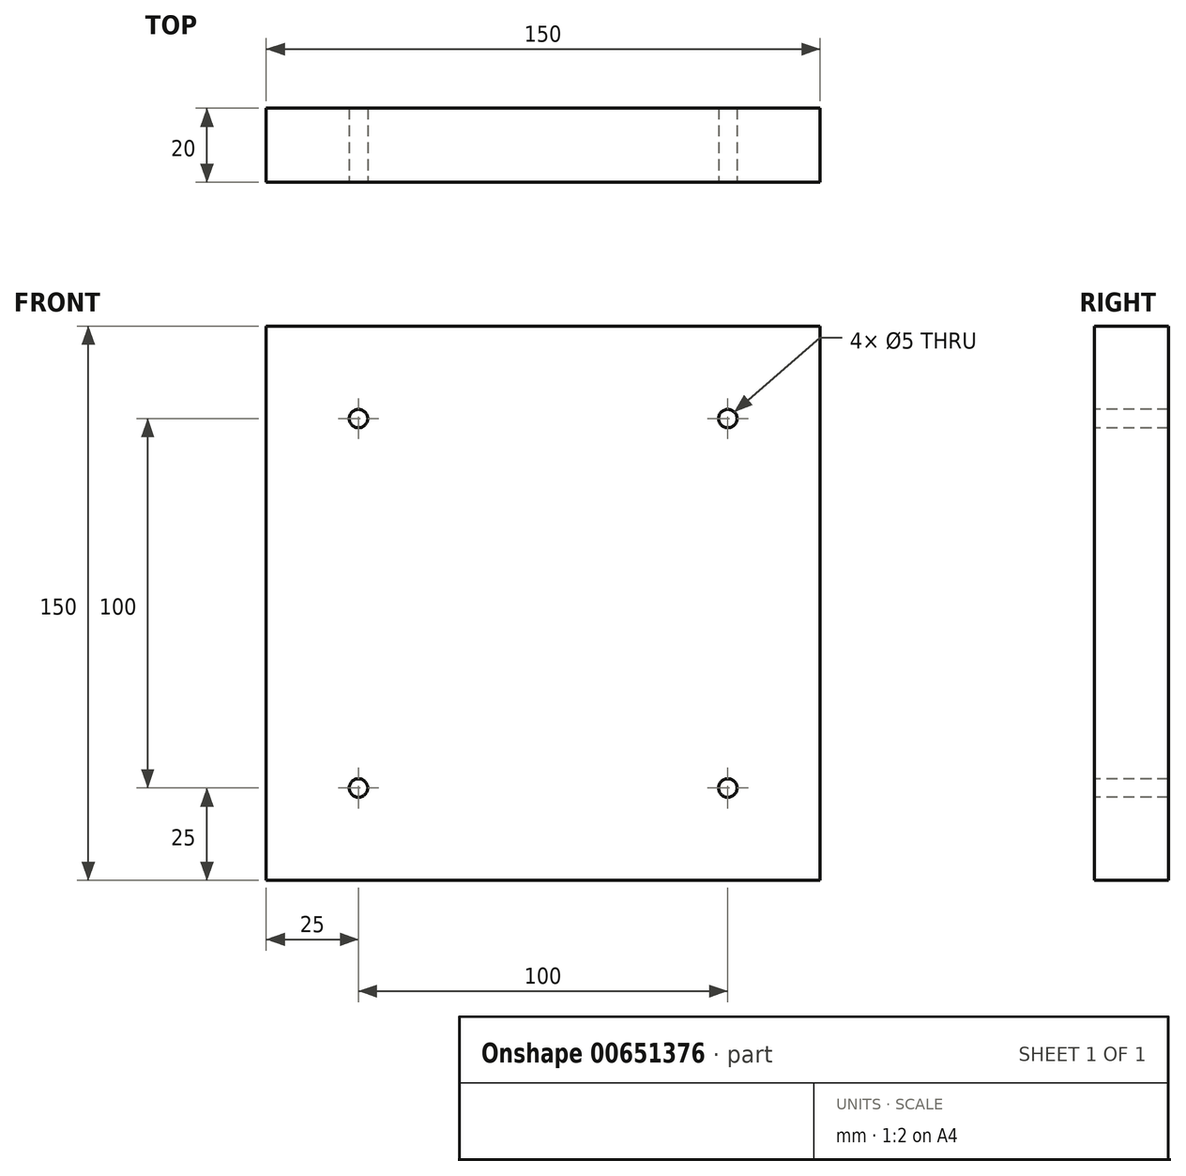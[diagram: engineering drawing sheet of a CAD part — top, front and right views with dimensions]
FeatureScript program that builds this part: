
annotation { "Feature Type Name" : "Feature", "Feature Type Description" : "" }
export const myFeature = defineFeature(function(context is Context, id is Id, definition is map)
    precondition{}
    {
        {
            var Q0;
            Q0=qCreatedBy(makeId("Front.planeOp"),FACE);
            var sketch = newSketch(context, id + "F0", { "sketchPlane" : qUnion([Q0])});
            skLineSegment(sketch, "E0.bottom", {"start": v(75, 75) * mm, "end": v(-75, 75) * mm});
            skLineSegment(sketch, "E0.top", {"start": v(75, -75) * mm, "end": v(-75, -75) * mm});
            skLineSegment(sketch, "E0.left", {"start": v(75, 75) * mm, "end": v(75, -75) * mm});
            skLineSegment(sketch, "E0.right", {"start": v(-75, 75) * mm, "end": v(-75, -75) * mm});
            skPoint(sketch, "E0.middle", {"position": v(0, 0) * mm});
            skSolve(sketch);
        }
        {
            var Q0;
            Q0 = qSketchRegion(id + "F0", true);
            extrude(context, id + "F1", {"entities" : qUnion([Q0]), "depth" : 20 * mm, "offsetDistance" : 25 * mm});
        }
        {
            var Q0;
            Q0=makeQuery(id+"F1.opExtrude","CAP_FACE",FACE,{"disambiguationData":[OSD([sQuery(id+"F0.wireOp",EDGE,"E0.bottom"),sQuery(id+"F0.wireOp",EDGE,"E0.top"),sQuery(id+"F0.wireOp",EDGE,"E0.left"),sQuery(id+"F0.wireOp",EDGE,"E0.right")])],"isStart":false});
            var sketch = newSketch(context, id + "F2", { "sketchPlane" : qUnion([Q0])});
            skLineSegment(sketch, "E1.bottom", {"start": v(50, 50) * mm, "end": v(-50, 50) * mm, "construction": true});
            skLineSegment(sketch, "E1.top", {"start": v(50, -50) * mm, "end": v(-50, -50) * mm, "construction": true});
            skLineSegment(sketch, "E1.left", {"start": v(50, 50) * mm, "end": v(50, -50) * mm, "construction": true});
            skLineSegment(sketch, "E1.right", {"start": v(-50, 50) * mm, "end": v(-50, -50) * mm, "construction": true});
            skPoint(sketch, "E1.middle", {"position": v(0, 0) * mm});
            skCircle(sketch, "E2", {"center": v(50, 50) * mm, "radius": 2.5 * mm});
            skCircle(sketch, "E3", {"center": v(50, -50) * mm, "radius": 2.5 * mm});
            skCircle(sketch, "E4", {"center": v(-50, -50) * mm, "radius": 2.5 * mm});
            skCircle(sketch, "E5", {"center": v(-50, 50) * mm, "radius": 2.5 * mm});
            skSolve(sketch);
        }
        {
            var Q0;
            Q0 = qSketchRegion(id + "F2", true);
            extrude(context, id + "F3", {"entities" : qUnion([Q0]), "operationType" : NewBodyOperationType.REMOVE, "endBound" : BoundingType.THROUGH_ALL, "oppositeDirection" : true, "depth" : 25 * mm, "offsetDistance" : 25 * mm});
        }
    });
